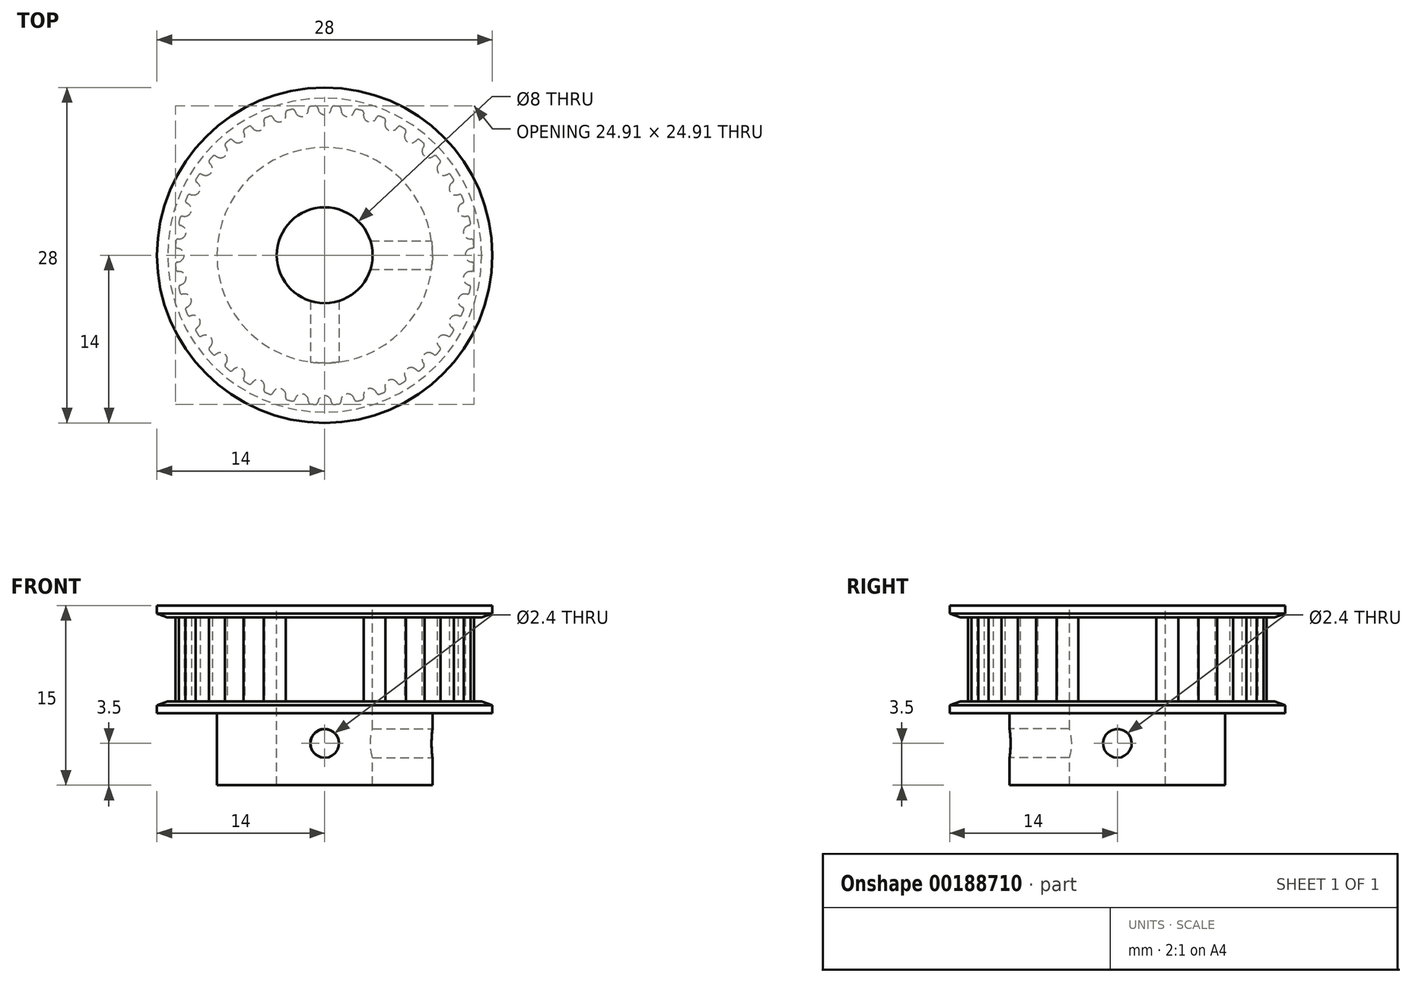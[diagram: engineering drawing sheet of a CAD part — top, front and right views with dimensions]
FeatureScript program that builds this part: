
annotation { "Feature Type Name" : "Feature", "Feature Type Description" : "" }
export const myFeature = defineFeature(function(context is Context, id is Id, definition is map)
    precondition{}
    {
        {
            assignVariable(context, id + "F0", {"name" : "teeth", "anyValue" : 40});
        }
        {
            assignVariable(context, id + "F1", {"name" : "belt_width", "anyValue" : 6 * mm});
        }
        {
            assignVariable(context, id + "F2", {"name" : "bore_diameter", "anyValue" : 8 * mm});
        }
        {
            var Q0;
            Q0=qCreatedBy(makeId("Top.planeOp"),FACE);
            var sketch = newSketch(context, id + "F3", { "sketchPlane" : qUnion([Q0])});
            skLineSegment(sketch, "E0", {"start": v(0, 0) * mm, "end": v(0, 11.73) * mm, "construction": true});
            skCircle(sketch, "E1", {"center": v(0, 0) * mm, "radius": 12.48 * mm});
            skPoint(sketch, "E2.MirrorCS.end.orphan", {"position": v(0.98, 12.44) * mm});
            skLineSegment(sketch, "E3", {"start": v(0.98, 12.44) * mm, "end": v(1, 12.7) * mm, "construction": true});
            skLineSegment(sketch, "E4", {"start": v(-0.98, 12.44) * mm, "end": v(-1, 12.7) * mm, "construction": true});
            skArc(sketch, "E5", {"start": v(0, 11.73) * mm, "mid": v(0.34, 11.84) * mm, "end": v(0.54, 12.14) * mm});
            skArc(sketch, "E6", {"start": v(0.54, 12.14) * mm, "mid": v(0.56, 12.23) * mm, "end": v(0.58, 12.33) * mm, "construction": true});
            skLineSegment(sketch, "E7", {"start": v(0, 11.73) * mm, "end": v(0, 12.48) * mm, "construction": true});
            skLineSegment(sketch, "E8", {"start": v(0, 12.48) * mm, "end": v(0, 12.73) * mm, "construction": true});
            skArc(sketch, "E9", {"start": v(0.58, 12.33) * mm, "mid": v(0.64, 12.42) * mm, "end": v(0.74, 12.46) * mm, "construction": true});
            skArc(sketch, "E10", {"start": v(1, 12.7) * mm, "mid": v(0, 12.73) * mm, "end": v(-1, 12.7) * mm, "construction": true});
            skLineSegment(sketch, "E11", {"start": v(0.98, 12.44) * mm, "end": v(0.92, 11.7) * mm});
            skLineSegment(sketch, "E12", {"start": v(0.92, 11.7) * mm, "end": v(0, 0) * mm});
            skLineSegment(sketch, "E13", {"start": v(0, 0) * mm, "end": v(-0.92, 11.7) * mm});
            skLineSegment(sketch, "E14", {"start": v(-0.92, 11.7) * mm, "end": v(-0.98, 12.44) * mm});
            skArc(sketch, "E15", {"start": v(0.77, 12.45) * mm, "mid": v(0.65, 12.42) * mm, "end": v(0.58, 12.31) * mm});
            skArc(sketch, "E16", {"start": v(0.54, 12.14) * mm, "mid": v(0.56, 12.22) * mm, "end": v(0.58, 12.31) * mm});
            skArc(sketch, "E17.MirrorCS", {"start": v(0, 11.73) * mm, "mid": v(-0.34, 11.84) * mm, "end": v(-0.54, 12.14) * mm});
            skArc(sketch, "E18.MirrorCS", {"start": v(-0.54, 12.14) * mm, "mid": v(-0.56, 12.22) * mm, "end": v(-0.58, 12.31) * mm});
            skArc(sketch, "E19.MirrorCS", {"start": v(-0.77, 12.45) * mm, "mid": v(-0.65, 12.42) * mm, "end": v(-0.58, 12.31) * mm});
            skArc(sketch, "E20", {"start": v(0, 12.48) * mm, "mid": v(-0.2, 12.48) * mm, "end": v(-0.4, 12.47) * mm});
            skArc(sketch, "E21", {"start": v(0.92, 11.7) * mm, "mid": v(0, 11.73) * mm, "end": v(-0.92, 11.7) * mm, "construction": true});
            skLineSegment(sketch, "E22", {"start": v(1, 12.7) * mm, "end": v(1.03, 13.07) * mm, "construction": true});
            skLineSegment(sketch, "E23", {"start": v(-1, 12.7) * mm, "end": v(-1.03, 13.07) * mm, "construction": true});
            skArc(sketch, "E24", {"start": v(-1.03, 13.07) * mm, "mid": v(0, 13.1) * mm, "end": v(1.03, 13.07) * mm, "construction": true});
            skSolve(sketch);
        }
        {
            var Q0;
            Q0=makeQuery(id+"F3.imprint","IMPRINT",FACE,{"disambiguationData":[TD([[makeQuery(id+"F3.imprint","IMPRINT",EDGE,{"derivedFrom":sQuery(id+"F3.wireOp",EDGE,"E5")}),-1.0]])]});
            var Q1;
            {var subQ1=sQuery(id+"F3.wireOp",EDGE,"E14");Q1=makeQuery(id+"F3.imprint","IMPRINT",FACE,{"disambiguationData":[TD([[makeQuery(id+"F3.imprint","IMPRINT",EDGE,{"derivedFrom":subQ1}),-1.0]])]});}
            var Q2;
            {var subQ0=sQuery(id+"F3.wireOp",EDGE,"E12");Q2=makeQuery(id+"F3.imprint","IMPRINT",FACE,{"disambiguationData":[TD([[makeQuery(id+"F3.imprint","IMPRINT",EDGE,{"derivedFrom":subQ0}),-1.0]])]});}
            extrude(context, id + "F4", {"entities" : qUnion([Q0, Q1, Q2]), "depth" : getVariable(context, 'belt_width') + 1 * mm, "symmetric" : true});
        }
        {
            var Q0;
            Q0=makeQuery(id+"F4.opExtrude","SWEPT_BODY",BODY,{"disambiguationData":[OSD([sQuery(id+"F3.wireOp",EDGE,"E1"),sQuery(id+"F3.wireOp",EDGE,"E5"),sQuery(id+"F3.wireOp",EDGE,"E11"),sQuery(id+"F3.wireOp",EDGE,"E12"),sQuery(id+"F3.wireOp",EDGE,"E13"),sQuery(id+"F3.wireOp",EDGE,"E14"),sQuery(id+"F3.wireOp",EDGE,"E15"),sQuery(id+"F3.wireOp",EDGE,"E16"),sQuery(id+"F3.wireOp",EDGE,"E17.MirrorCS"),sQuery(id+"F3.wireOp",EDGE,"E18.MirrorCS"),sQuery(id+"F3.wireOp",EDGE,"E19.MirrorCS")])]});
            var Q1;
            Q1=makeQuery(id+"F4.opExtrude","SWEPT_EDGE",EDGE,{"disambiguationData":[OSD([sQuery(id+"F3.wireOp",EDGE,"E12"),sQuery(id+"F3.wireOp",EDGE,"E13")])]});
            circularPattern(context, id + "F5", {"operationType" : NewBodyOperationType.ADD, "entities" : qUnion([Q0]), "axis" : qUnion([Q1]), "angle" : 360 * degree, "instanceCount" : getVariable(context, 'teeth'), "equalSpace" : true, "computeTransformsWithoutBuiltin" : true});
        }
        {
            var Q0;
            Q0=qCreatedBy(makeId("Front.planeOp"),FACE);
            var sketch = newSketch(context, id + "F6", { "sketchPlane" : qUnion([Q0])});
            skLineSegment(sketch, "E25", {"start": v(0, -3.5) * mm, "end": v(13.1, -3.5) * mm});
            skLineSegment(sketch, "E26", {"start": v(13.1, -3.5) * mm, "end": v(14, -3.82) * mm});
            skLineSegment(sketch, "E27", {"start": v(9, -10.5) * mm, "end": v(0, -10.5) * mm});
            skLineSegment(sketch, "E28", {"start": v(0, 3.5) * mm, "end": v(13.1, 3.5) * mm});
            skLineSegment(sketch, "E29", {"start": v(14, 3.82) * mm, "end": v(13.1, 3.5) * mm});
            skLineSegment(sketch, "E30", {"start": v(14, 3.82) * mm, "end": v(14, 4.5) * mm});
            skLineSegment(sketch, "E31", {"start": v(14, 4.5) * mm, "end": v(0, 4.5) * mm});
            skLineSegment(sketch, "E32", {"start": v(0, 4.5) * mm, "end": v(0, 3.5) * mm});
            skLineSegment(sketch, "E33", {"start": v(13.1, -3.5) * mm, "end": v(14, -3.5) * mm, "construction": true});
            skLineSegment(sketch, "E34", {"start": v(14, -3.5) * mm, "end": v(14, -3.82) * mm, "construction": true});
            skLineSegment(sketch, "E35", {"start": v(13.1, 3.5) * mm, "end": v(14, 3.5) * mm, "construction": true});
            skLineSegment(sketch, "E36", {"start": v(14, 3.5) * mm, "end": v(14, 3.82) * mm, "construction": true});
            skLineSegment(sketch, "E37", {"start": v(12.48, 0) * mm, "end": v(12.48, -3.5) * mm, "construction": true});
            skLineSegment(sketch, "E38", {"start": v(14, -4.5) * mm, "end": v(0, -4.5) * mm});
            skLineSegment(sketch, "E39", {"start": v(14, -3.82) * mm, "end": v(14, -4.5) * mm});
            skLineSegment(sketch, "E40", {"start": v(0, -3.5) * mm, "end": v(0, -4.5) * mm});
            skLineSegment(sketch, "E41", {"start": v(9, -10.5) * mm, "end": v(9, -4.5) * mm});
            skLineSegment(sketch, "E42", {"start": v(0, -10.5) * mm, "end": v(0, -4.5) * mm});
            skSolve(sketch);
        }
        {
            var Q0;
            Q0=makeQuery(id+"F6.imprint","IMPRINT",FACE,{"disambiguationData":[TD([[makeQuery(id+"F6.imprint","IMPRINT",EDGE,{"derivedFrom":sQuery(id+"F6.wireOp",EDGE,"E28")}),1.0]])]});
            var Q1;
            Q1=makeQuery(id+"F6.imprint","IMPRINT",FACE,{"disambiguationData":[TD([[makeQuery(id+"F6.imprint","IMPRINT",EDGE,{"derivedFrom":sQuery(id+"F6.wireOp",EDGE,"E25")}),-1.0]])]});
            var Q2;
            Q2=makeQuery(id+"F6.imprint","IMPRINT",FACE,{"disambiguationData":[TD([[makeQuery(id+"F6.imprint","IMPRINT",EDGE,{"derivedFrom":sQuery(id+"F6.wireOp",EDGE,"E27")}),-1.0]])]});
            var Q3;
            Q3=qConstructionFilter(qBodyType(qCreatedBy(id+"F6",EDGE),BodyType.WIRE),ConstructionObject.NO);
            var Q4;
            Q4=sQuery(id+"F6.wireOp",EDGE,"E42");
            revolve(context, id + "F7", {"operationType" : NewBodyOperationType.ADD, "entities" : qUnion([Q0, Q1, Q2]), "surfaceEntities" : qUnion([Q3]), "axis" : qUnion([Q4]), "revolveType" : RevolveType.FULL});
        }
        {
            var Q0;
            Q0=makeQuery(id+"F7.opRevolve","SWEPT_FACE",FACE,{"disambiguationData":[OSD([sQuery(id+"F6.wireOp",EDGE,"E27")])]});
            var sketch = newSketch(context, id + "F8", { "sketchPlane" : qUnion([Q0])});
            skPoint(sketch, "E43", {"position": v(0, 0) * mm});
            skSolve(sketch);
        }
        {
            var Q0;
            Q0=sQuery(id+"F8.wireOp",VERTEX,"E43");
            var Q1;
            Q1=makeQuery(id+"F4.opExtrude","SWEPT_BODY",BODY,{"disambiguationData":[OSD([sQuery(id+"F3.wireOp",EDGE,"E1"),sQuery(id+"F3.wireOp",EDGE,"E5"),sQuery(id+"F3.wireOp",EDGE,"E11"),sQuery(id+"F3.wireOp",EDGE,"E12"),sQuery(id+"F3.wireOp",EDGE,"E13"),sQuery(id+"F3.wireOp",EDGE,"E14"),sQuery(id+"F3.wireOp",EDGE,"E15"),sQuery(id+"F3.wireOp",EDGE,"E16"),sQuery(id+"F3.wireOp",EDGE,"E17.MirrorCS"),sQuery(id+"F3.wireOp",EDGE,"E18.MirrorCS"),sQuery(id+"F3.wireOp",EDGE,"E19.MirrorCS")])]});
            hole(context, id + "F9", {"style" : HoleStyle.SIMPLE, "holeDiameter" : getVariable(context, 'bore_diameter'), "endStyle" : HoleEndStyle.THROUGH, "locations" : qUnion([Q0]), "scope" : qUnion([Q1]), "isTappedThrough" : true, "startStyle" : HoleStartStyle.PART});
        }
        {
            var Q0;
            Q0=qCreatedBy(makeId("Front.planeOp"),FACE);
            var sketch = newSketch(context, id + "F10", { "sketchPlane" : qUnion([Q0])});
            skPoint(sketch, "E44", {"position": v(0, -7) * mm});
            skLineSegment(sketch, "E45", {"start": v(0, -10.5) * mm, "end": v(0, -3.5) * mm});
            skSolve(sketch);
        }
        {
            var Q0;
            Q0=qCreatedBy(makeId("Right.planeOp"),FACE);
            var sketch = newSketch(context, id + "F11", { "sketchPlane" : qUnion([Q0])});
            skPoint(sketch, "E46", {"position": v(0, -7) * mm});
            skSolve(sketch);
        }
        {
            var Q0;
            Q0=sQuery(id+"F10.wireOp",VERTEX,"E44");
            var Q1;
            Q1=makeQuery(id+"F4.opExtrude","SWEPT_BODY",BODY,{"disambiguationData":[OSD([sQuery(id+"F3.wireOp",EDGE,"E1"),sQuery(id+"F3.wireOp",EDGE,"E5"),sQuery(id+"F3.wireOp",EDGE,"E11"),sQuery(id+"F3.wireOp",EDGE,"E12"),sQuery(id+"F3.wireOp",EDGE,"E13"),sQuery(id+"F3.wireOp",EDGE,"E14"),sQuery(id+"F3.wireOp",EDGE,"E15"),sQuery(id+"F3.wireOp",EDGE,"E16"),sQuery(id+"F3.wireOp",EDGE,"E17.MirrorCS"),sQuery(id+"F3.wireOp",EDGE,"E18.MirrorCS"),sQuery(id+"F3.wireOp",EDGE,"E19.MirrorCS")])]});
            hole(context, id + "F12", {"style" : HoleStyle.SIMPLE, "endStyle" : HoleEndStyle.THROUGH, "oppositeDirection" : true, "standardTappedOrClearance" : lookupTablePath({ "standard" : "ISO", "engagement" : "75%", "pitch" : "0.6 mm", "size" : "M3", "type" : "Tapped" }), "standardBlindInLast" : lookupTablePath({ "standard" : "ISO", "engagement" : "75%", "pitch" : "0.6 mm", "size" : "M3", "type" : "Tapped" }), "holeDiameter" : 2.4 * mm, "locations" : qUnion([Q0]), "scope" : qUnion([Q1]), "isTappedThrough" : true, "showTappedDepth" : true, "startStyle" : HoleStartStyle.PART});
        }
        {
            var Q0;
            Q0=sQuery(id+"F11.wireOp",VERTEX,"E46");
            var Q1;
            Q1=makeQuery(id+"F4.opExtrude","SWEPT_BODY",BODY,{"disambiguationData":[OSD([sQuery(id+"F3.wireOp",EDGE,"E1"),sQuery(id+"F3.wireOp",EDGE,"E5"),sQuery(id+"F3.wireOp",EDGE,"E11"),sQuery(id+"F3.wireOp",EDGE,"E12"),sQuery(id+"F3.wireOp",EDGE,"E13"),sQuery(id+"F3.wireOp",EDGE,"E14"),sQuery(id+"F3.wireOp",EDGE,"E15"),sQuery(id+"F3.wireOp",EDGE,"E16"),sQuery(id+"F3.wireOp",EDGE,"E17.MirrorCS"),sQuery(id+"F3.wireOp",EDGE,"E18.MirrorCS"),sQuery(id+"F3.wireOp",EDGE,"E19.MirrorCS")])]});
            hole(context, id + "F13", {"style" : HoleStyle.SIMPLE, "endStyle" : HoleEndStyle.THROUGH, "oppositeDirection" : true, "standardTappedOrClearance" : lookupTablePath({ "standard" : "ISO", "engagement" : "75%", "pitch" : "0.6 mm", "size" : "M3", "type" : "Tapped" }), "standardBlindInLast" : lookupTablePath({ "standard" : "ISO", "engagement" : "75%", "pitch" : "0.6 mm", "size" : "M3", "type" : "Tapped" }), "holeDiameter" : 2.4 * mm, "locations" : qUnion([Q0]), "scope" : qUnion([Q1]), "isTappedThrough" : true, "showTappedDepth" : true, "startStyle" : HoleStartStyle.PART});
        }
    });
